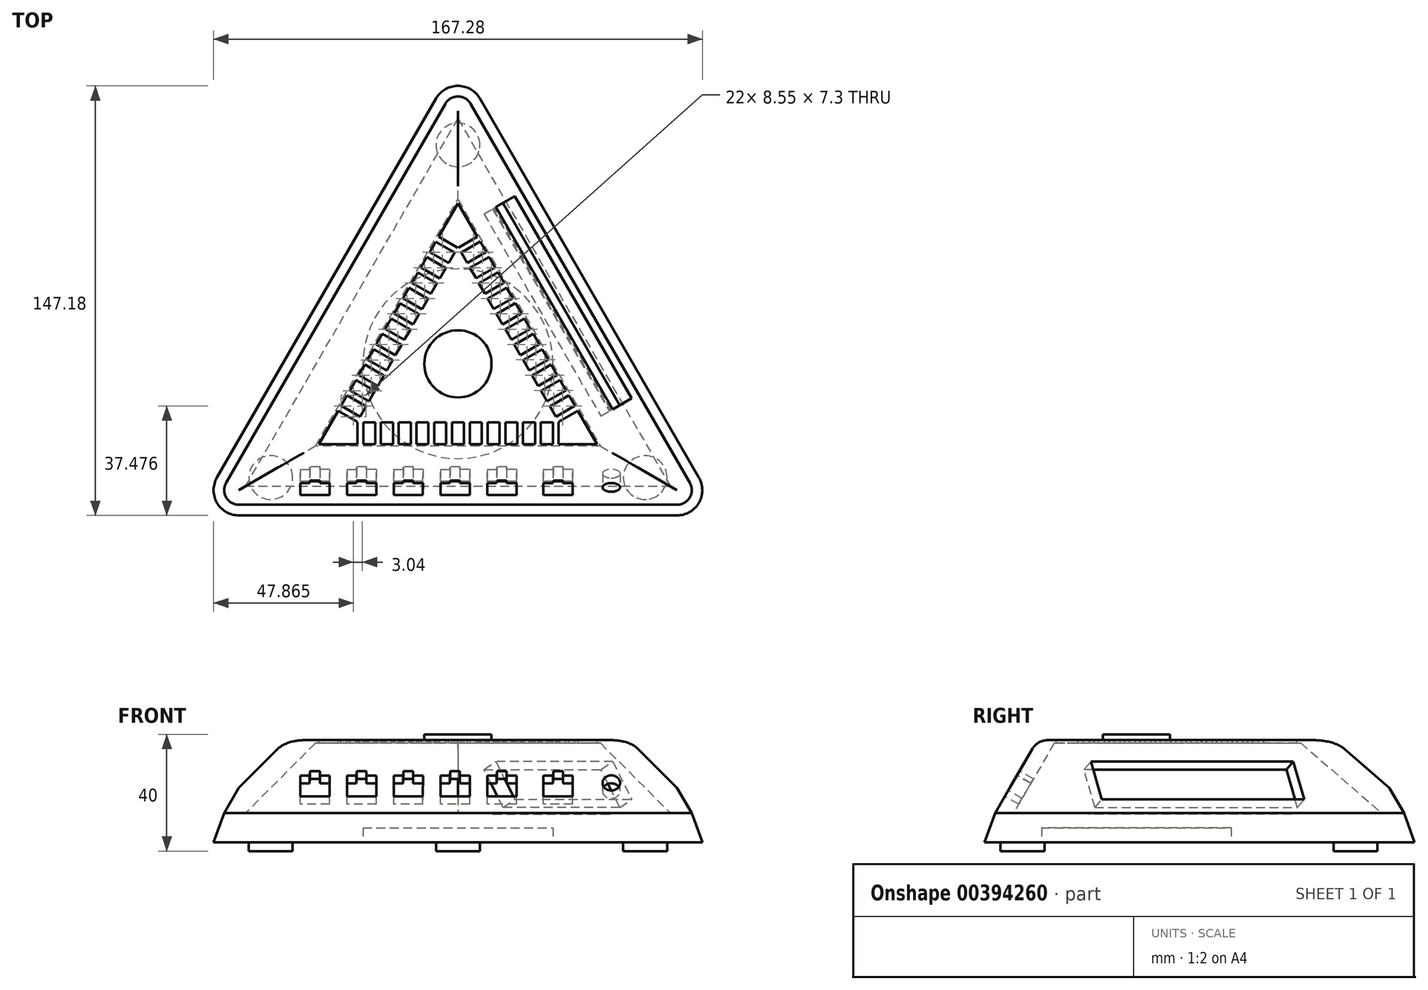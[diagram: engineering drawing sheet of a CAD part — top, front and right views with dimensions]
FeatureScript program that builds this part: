
annotation { "Feature Type Name" : "Feature", "Feature Type Description" : "" }
export const myFeature = defineFeature(function(context is Context, id is Id, definition is map)
    precondition{}
    {
        {
            var Q0;
            Q0=qCreatedBy(makeId("Top.planeOp"),FACE);
            var sketch = newSketch(context, id + "F0", { "sketchPlane" : qUnion([Q0])});
            skCircle(sketch, "E0.cCircle", {"center": v(0, 0) * mm, "radius": 48.3 * mm, "construction": true});
            skLineSegment(sketch, "E0.0", {"start": v(75, -48.3) * mm, "end": v(-75, -48.3) * mm});
            skLineSegment(sketch, "E0.1", {"start": v(-79.33, -40.8) * mm, "end": v(-4.33, 89.1) * mm});
            skLineSegment(sketch, "E0.2", {"start": v(4.33, 89.1) * mm, "end": v(79.33, -40.8) * mm});
            skPoint(sketch, "E0.0.midPoint", {"position": v(0, -48.3) * mm});
            skPoint(sketch, "E1.visualSharp", {"position": v(0, 96.6) * mm});
            skArc(sketch, "E1.filletArc", {"start": v(4.33, 89.1) * mm, "mid": v(0, 91.6) * mm, "end": v(-4.33, 89.1) * mm});
            skPoint(sketch, "E2.visualSharp", {"position": v(83.66, -48.3) * mm});
            skArc(sketch, "E2.filletArc", {"start": v(75, -48.3) * mm, "mid": v(79.33, -45.8) * mm, "end": v(79.33, -40.8) * mm});
            skPoint(sketch, "E3.visualSharp", {"position": v(-83.66, -48.3) * mm});
            skArc(sketch, "E3.filletArc", {"start": v(-79.33, -40.8) * mm, "mid": v(-79.33, -45.8) * mm, "end": v(-75, -48.3) * mm});
            skSolve(sketch);
        }
        {
            var Q0;
            Q0=makeQuery(id+"F0.imprint","IMPRINT",FACE,{"disambiguationData":[TD([[makeQuery(id+"F0.imprint","IMPRINT",EDGE,{"derivedFrom":sQuery(id+"F0.wireOp",EDGE,"E0.0")}),-1.0]])]});
            extrude(context, id + "F1", {"entities" : qUnion([Q0]), "depth" : 25 * mm, "hasDraft" : true, "draftAngle" : 30 * degree, "draftPullDirection" : true, "hasSecondDirection" : true, "secondDirectionOppositeDirection" : true, "secondDirectionDepth" : 10 * mm, "hasSecondDirectionDraft" : true, "secondDirectionDraftAngle" : 20 * degree});
        }
        {
            var Q0;
            Q0=makeQuery(id+"F1.opExtrude","CAP_EDGE",EDGE,{"disambiguationData":[OSD([sQuery(id+"F0.wireOp",EDGE,"E0.0")])],"isStart":false});
            var Q1;
            Q1=makeQuery(id+"F1.opExtrude","CAP_EDGE",EDGE,{"disambiguationData":[OSD([sQuery(id+"F0.wireOp",EDGE,"E0.2")])],"isStart":false});
            var Q2;
            Q2=makeQuery(id+"F1.opExtrude","CAP_EDGE",EDGE,{"disambiguationData":[OSD([sQuery(id+"F0.wireOp",EDGE,"E0.1")])],"isStart":false});
            fillet(context, id + "F2", {"entities" : qUnion([Q0, Q1, Q2]), "radius" : 6 * mm, "tangentPropagation" : true, "allowEdgeOverflow" : false});
        }
        {
            var Q0;
            Q0=makeQuery(id+"F1.opExtrude","CAP_FACE",FACE,{"disambiguationData":[OSD([sQuery(id+"F0.wireOp",EDGE,"E0.0"),sQuery(id+"F0.wireOp",EDGE,"E0.1"),sQuery(id+"F0.wireOp",EDGE,"E0.2"),sQuery(id+"F0.wireOp",EDGE,"E1.filletArc"),sQuery(id+"F0.wireOp",EDGE,"E2.filletArc"),sQuery(id+"F0.wireOp",EDGE,"E3.filletArc")])],"isStart":false});
            var sketch = newSketch(context, id + "F3", { "sketchPlane" : qUnion([Q0])});
            skCircle(sketch, "E4", {"center": v(0, 0) * mm, "radius": 11.5 * mm});
            skCircle(sketch, "E5.cCircle", {"center": v(0, 0) * mm, "radius": 20 * mm, "construction": true});
            skLineSegment(sketch, "E5.0", {"start": v(34.64, -20) * mm, "end": v(-34.64, -20) * mm});
            skLineSegment(sketch, "E5.1", {"start": v(-34.64, -20) * mm, "end": v(0, 40) * mm});
            skLineSegment(sketch, "E5.2", {"start": v(0, 40) * mm, "end": v(34.64, -20) * mm});
            skPoint(sketch, "E5.0.midPoint", {"position": v(0, -20) * mm});
            skCircle(sketch, "E6.cCircle", {"center": v(0, 0) * mm, "radius": 27.5 * mm, "construction": true});
            skLineSegment(sketch, "E6.0", {"start": v(47.63, -27.5) * mm, "end": v(-47.63, -27.5) * mm});
            skLineSegment(sketch, "E6.1", {"start": v(-47.63, -27.5) * mm, "end": v(0, 55) * mm});
            skLineSegment(sketch, "E6.2", {"start": v(0, 55) * mm, "end": v(47.63, -27.5) * mm});
            skPoint(sketch, "E6.0.midPoint", {"position": v(0, -27.5) * mm});
            skSolve(sketch);
        }
        {
            var Q0;
            Q0=makeQuery(id+"F3.imprint","IMPRINT",FACE,{"disambiguationData":[TD([[makeQuery(id+"F3.imprint","IMPRINT",EDGE,{"derivedFrom":sQuery(id+"F3.wireOp",EDGE,"E4")}),1.0]])]});
            extrude(context, id + "F4", {"entities" : qUnion([Q0]), "operationType" : NewBodyOperationType.ADD, "depth" : 2 * mm});
        }
        {
            var Q0;
            Q0=makeQuery(id+"F4.opExtrude","CAP_FACE",FACE,{"disambiguationData":[OSD([sQuery(id+"F3.wireOp",EDGE,"E4")])],"isStart":false});
            var sketch = newSketch(context, id + "F5", { "sketchPlane" : qUnion([Q0])});
            skSolve(sketch);
        }
        {
            var Q0;
            Q0=makeQuery(id+"F1.opExtrude","CAP_FACE",FACE,{"disambiguationData":[OSD([sQuery(id+"F0.wireOp",EDGE,"E0.0"),sQuery(id+"F0.wireOp",EDGE,"E0.1"),sQuery(id+"F0.wireOp",EDGE,"E0.2"),sQuery(id+"F0.wireOp",EDGE,"E1.filletArc"),sQuery(id+"F0.wireOp",EDGE,"E2.filletArc"),sQuery(id+"F0.wireOp",EDGE,"E3.filletArc")])],"isStart":true});
            var sketch = newSketch(context, id + "F6", { "sketchPlane" : qUnion([Q0])});
            skCircle(sketch, "E7", {"center": v(-64.07, 38.98) * mm, "radius": 7.5 * mm});
            skPoint(sketch, "E8.orphan", {"position": v(0, 0) * mm});
            skPoint(sketch, "E9.orphan", {"position": v(-82.48, 47.62) * mm});
            skCircle(sketch, "E10.MirrorC", {"center": v(64.07, 38.98) * mm, "radius": 7.5 * mm});
            skLineSegment(sketch, "E11", {"start": v(-64.07, 38.98) * mm, "end": v(0, 0) * mm});
            skCircle(sketch, "E12", {"center": v(0, -75) * mm, "radius": 7.5 * mm});
            skPoint(sketch, "E13.end.orphan", {"position": v(0, -95.24) * mm});
            skSolve(sketch);
        }
        {
            var Q0;
            Q0 = qSketchRegion(id + "F6", true);
            extrude(context, id + "F7", {"entities" : qUnion([Q0]), "operationType" : NewBodyOperationType.ADD, "depth" : 3 * mm});
        }
        {
            var Q0;
            Q0=makeQuery(id+"F1.opExtrude","CAP_FACE",FACE,{"disambiguationData":[OSD([sQuery(id+"F0.wireOp",EDGE,"E0.0"),sQuery(id+"F0.wireOp",EDGE,"E0.1"),sQuery(id+"F0.wireOp",EDGE,"E0.2"),sQuery(id+"F0.wireOp",EDGE,"E1.filletArc"),sQuery(id+"F0.wireOp",EDGE,"E2.filletArc"),sQuery(id+"F0.wireOp",EDGE,"E3.filletArc")])],"isStart":true});
            var sketch = newSketch(context, id + "F8", { "sketchPlane" : qUnion([Q0])});
            skCircle(sketch, "E14", {"center": v(0, 0) * mm, "radius": 32.5 * mm});
            skSolve(sketch);
        }
        {
            var Q0;
            Q0 = qSketchRegion(id + "F8", true);
            extrude(context, id + "F9", {"entities" : qUnion([Q0]), "operationType" : NewBodyOperationType.REMOVE, "oppositeDirection" : true, "depth" : 5 * mm});
        }
        {
            var Q0;
            Q0=makeQuery(id+"F1.*.split.splitOp","SPLIT",FACE,{"derivedFrom":makeQuery(id+"F1.opExtrude","SWEPT_FACE",FACE,{"disambiguationData":[OSD([sQuery(id+"F0.wireOp",EDGE,"E0.0")])]})});
            var sketch = newSketch(context, id + "F10", { "sketchPlane" : qUnion([Q0])});
            skLineSegment(sketch, "E15.top", {"start": v(-53.99, -17.5) * mm, "end": v(-43.99, -17.5) * mm});
            skLineSegment(sketch, "E16", {"start": v(-53.99, -9.3) * mm, "end": v(-53.99, -17.5) * mm});
            skLineSegment(sketch, "E17", {"start": v(-43.96, -9.24) * mm, "end": v(-43.99, -17.5) * mm});
            skLineSegment(sketch, "E18", {"start": v(-50.6, -7.5) * mm, "end": v(-47.3, -7.5) * mm});
            skLineSegment(sketch, "E19", {"start": v(-50.6, -7.5) * mm, "end": v(-50.74, -9.3) * mm});
            skLineSegment(sketch, "E20", {"start": v(-50.74, -9.3) * mm, "end": v(-53.99, -9.3) * mm});
            skLineSegment(sketch, "E21", {"start": v(-47.3, -7.5) * mm, "end": v(-47.3, -9.3) * mm});
            skLineSegment(sketch, "E22", {"start": v(-47.3, -9.3) * mm, "end": v(-43.96, -9.24) * mm});
            skPoint(sketch, "E15.left.start.orphan", {"position": v(-53.99, -7.5) * mm});
            skPoint(sketch, "E15.right.start.orphan", {"position": v(-43.99, -7.5) * mm});
            skLineSegment(sketch, "E23.1.0.0", {"start": v(-37.99, -9.3) * mm, "end": v(-37.99, -17.5) * mm});
            skLineSegment(sketch, "E23.1.0.1", {"start": v(-27.96, -9.24) * mm, "end": v(-27.99, -17.5) * mm});
            skPoint(sketch, "E23.1.0.2", {"position": v(-37.99, -7.5) * mm});
            skPoint(sketch, "E23.1.0.3", {"position": v(-27.99, -7.5) * mm});
            skLineSegment(sketch, "E23.1.0.4", {"start": v(-37.99, -17.5) * mm, "end": v(-27.99, -17.5) * mm});
            skLineSegment(sketch, "E23.1.0.5", {"start": v(-34.6, -7.5) * mm, "end": v(-31.3, -7.5) * mm});
            skLineSegment(sketch, "E23.1.0.6", {"start": v(-31.3, -7.5) * mm, "end": v(-31.3, -9.3) * mm});
            skLineSegment(sketch, "E23.1.0.7", {"start": v(-34.6, -7.5) * mm, "end": v(-34.74, -9.3) * mm});
            skLineSegment(sketch, "E23.1.0.8", {"start": v(-34.74, -9.3) * mm, "end": v(-37.99, -9.3) * mm});
            skLineSegment(sketch, "E23.1.0.9", {"start": v(-31.3, -9.3) * mm, "end": v(-27.96, -9.24) * mm});
            skLineSegment(sketch, "E23.2.0.0", {"start": v(-21.99, -9.3) * mm, "end": v(-21.99, -17.5) * mm});
            skLineSegment(sketch, "E23.2.0.1", {"start": v(-11.96, -9.24) * mm, "end": v(-11.99, -17.5) * mm});
            skPoint(sketch, "E23.2.0.2", {"position": v(-21.99, -7.5) * mm});
            skPoint(sketch, "E23.2.0.3", {"position": v(-11.99, -7.5) * mm});
            skLineSegment(sketch, "E23.2.0.4", {"start": v(-21.99, -17.5) * mm, "end": v(-11.99, -17.5) * mm});
            skLineSegment(sketch, "E23.2.0.5", {"start": v(-18.6, -7.5) * mm, "end": v(-15.3, -7.5) * mm});
            skLineSegment(sketch, "E23.2.0.6", {"start": v(-15.3, -7.5) * mm, "end": v(-15.3, -9.3) * mm});
            skLineSegment(sketch, "E23.2.0.7", {"start": v(-18.6, -7.5) * mm, "end": v(-18.74, -9.3) * mm});
            skLineSegment(sketch, "E23.2.0.8", {"start": v(-18.74, -9.3) * mm, "end": v(-21.99, -9.3) * mm});
            skLineSegment(sketch, "E23.2.0.9", {"start": v(-15.3, -9.3) * mm, "end": v(-11.96, -9.24) * mm});
            skLineSegment(sketch, "E23.3.0.0", {"start": v(-5.99, -9.3) * mm, "end": v(-5.99, -17.5) * mm});
            skLineSegment(sketch, "E23.3.0.1", {"start": v(4.04, -9.24) * mm, "end": v(4.01, -17.5) * mm});
            skPoint(sketch, "E23.3.0.2", {"position": v(-5.99, -7.5) * mm});
            skPoint(sketch, "E23.3.0.3", {"position": v(4.01, -7.5) * mm});
            skLineSegment(sketch, "E23.3.0.4", {"start": v(-5.99, -17.5) * mm, "end": v(4.01, -17.5) * mm});
            skLineSegment(sketch, "E23.3.0.5", {"start": v(-2.6, -7.5) * mm, "end": v(0.7, -7.5) * mm});
            skLineSegment(sketch, "E23.3.0.6", {"start": v(0.7, -7.5) * mm, "end": v(0.7, -9.3) * mm});
            skLineSegment(sketch, "E23.3.0.7", {"start": v(-2.6, -7.5) * mm, "end": v(-2.74, -9.3) * mm});
            skLineSegment(sketch, "E23.3.0.8", {"start": v(-2.74, -9.3) * mm, "end": v(-5.99, -9.3) * mm});
            skLineSegment(sketch, "E23.3.0.9", {"start": v(0.7, -9.3) * mm, "end": v(4.04, -9.24) * mm});
            skLineSegment(sketch, "E23.4.0.0", {"start": v(10.01, -9.3) * mm, "end": v(10.01, -17.5) * mm});
            skLineSegment(sketch, "E23.4.0.1", {"start": v(20.04, -9.24) * mm, "end": v(20.01, -17.5) * mm});
            skPoint(sketch, "E23.4.0.2", {"position": v(10.01, -7.5) * mm});
            skPoint(sketch, "E23.4.0.3", {"position": v(20.01, -7.5) * mm});
            skLineSegment(sketch, "E23.4.0.4", {"start": v(10.01, -17.5) * mm, "end": v(20.01, -17.5) * mm});
            skLineSegment(sketch, "E23.4.0.5", {"start": v(13.4, -7.5) * mm, "end": v(16.7, -7.5) * mm});
            skLineSegment(sketch, "E23.4.0.6", {"start": v(16.7, -7.5) * mm, "end": v(16.7, -9.3) * mm});
            skLineSegment(sketch, "E23.4.0.7", {"start": v(13.4, -7.5) * mm, "end": v(13.26, -9.3) * mm});
            skLineSegment(sketch, "E23.4.0.8", {"start": v(13.26, -9.3) * mm, "end": v(10.01, -9.3) * mm});
            skLineSegment(sketch, "E23.4.0.9", {"start": v(16.7, -9.3) * mm, "end": v(20.04, -9.24) * mm});
            skLineSegment(sketch, "E23.5.0.0", {"start": v(29.26, -9.3) * mm, "end": v(29.26, -17.5) * mm});
            skLineSegment(sketch, "E23.5.0.1", {"start": v(39.3, -9.24) * mm, "end": v(39.26, -17.5) * mm});
            skPoint(sketch, "E23.5.0.2", {"position": v(29.26, -7.5) * mm});
            skPoint(sketch, "E23.5.0.3", {"position": v(39.26, -7.5) * mm});
            skLineSegment(sketch, "E23.5.0.4", {"start": v(29.26, -17.5) * mm, "end": v(39.26, -17.5) * mm});
            skLineSegment(sketch, "E23.5.0.5", {"start": v(32.64, -7.5) * mm, "end": v(35.95, -7.5) * mm});
            skLineSegment(sketch, "E23.5.0.6", {"start": v(35.95, -7.5) * mm, "end": v(35.95, -9.3) * mm});
            skLineSegment(sketch, "E23.5.0.7", {"start": v(32.64, -7.5) * mm, "end": v(32.5, -9.3) * mm});
            skLineSegment(sketch, "E23.5.0.8", {"start": v(32.5, -9.3) * mm, "end": v(29.26, -9.3) * mm});
            skLineSegment(sketch, "E23.5.0.9", {"start": v(35.95, -9.3) * mm, "end": v(39.3, -9.24) * mm});
            skLineSegment(sketch, "E23.direction1", {"start": v(-53.99, -17.5) * mm, "end": v(-37.99, -17.5) * mm, "construction": true});
            skCircle(sketch, "E24", {"center": v(52.49, -12.2) * mm, "radius": 3 * mm});
            skSolve(sketch);
        }
        {
            var Q0;
            Q0 = qSketchRegion(id + "F10", true);
            extrude(context, id + "F11", {"entities" : qUnion([Q0]), "operationType" : NewBodyOperationType.REMOVE, "oppositeDirection" : true, "depth" : 2 * mm});
        }
        {
            var Q0;
            Q0=qCreatedBy(makeId("Front.planeOp"),FACE);
            var sketch = newSketch(context, id + "F12", { "sketchPlane" : qUnion([Q0])});
            skLineSegment(sketch, "E25", {"start": v(0, 27.54) * mm, "end": v(0, -12.74) * mm});
            skSolve(sketch);
        }
        {
            var Q0;
            Q0 = qSketchRegion(id + "F3", true);
            extrude(context, id + "F13", {"entities" : qUnion([Q0]), "operationType" : NewBodyOperationType.REMOVE, "oppositeDirection" : true, "depth" : 5 * mm});
        }
        {
            var Q0;
            Q0=makeQuery(id+"F13.boolean.opBoolean","SPLIT",FACE,{"disambiguationData":[TD([makeQuery(id+"F4.opExtrude","SWEPT_FACE",FACE,{"disambiguationData":[OSD([sQuery(id+"F3.wireOp",EDGE,"E4")])]})])],"derivedFrom":makeQuery(id+"F1.opExtrude","CAP_FACE",FACE,{"disambiguationData":[OSD([sQuery(id+"F0.wireOp",EDGE,"E0.0"),sQuery(id+"F0.wireOp",EDGE,"E0.1"),sQuery(id+"F0.wireOp",EDGE,"E0.2"),sQuery(id+"F0.wireOp",EDGE,"E1.filletArc"),sQuery(id+"F0.wireOp",EDGE,"E2.filletArc"),sQuery(id+"F0.wireOp",EDGE,"E3.filletArc")])],"isStart":false})});
            cPlane(context, id + "F14", {"entities" : qUnion([Q0]), "cplaneType" : CPlaneType.OFFSET, "offset" : 0 * mm, "oppositeDirection" : true, "width" : 150 * mm, "height" : 150 * mm});
        }
        {
            var Q0;
            Q0=qCreatedBy(id+"F14.planeOp",FACE);
            var sketch = newSketch(context, id + "F15", { "sketchPlane" : qUnion([Q0])});
            skLineSegment(sketch, "E26.bottom", {"start": v(-34.42, -19.8) * mm, "end": v(-32.44, -19.8) * mm});
            skLineSegment(sketch, "E26.top", {"start": v(-34.42, -28.4) * mm, "end": v(-32.44, -28.4) * mm});
            skLineSegment(sketch, "E26.left", {"start": v(-34.42, -19.8) * mm, "end": v(-34.42, -28.4) * mm});
            skLineSegment(sketch, "E26.right", {"start": v(-32.44, -19.8) * mm, "end": v(-32.44, -28.4) * mm});
            skLineSegment(sketch, "E27.1.0.0", {"start": v(-26.36, -19.8) * mm, "end": v(-26.36, -28.4) * mm});
            skLineSegment(sketch, "E27.1.0.1", {"start": v(-28.34, -19.8) * mm, "end": v(-28.34, -28.4) * mm});
            skLineSegment(sketch, "E27.1.0.2", {"start": v(-28.34, -28.4) * mm, "end": v(-26.36, -28.4) * mm});
            skLineSegment(sketch, "E27.1.0.3", {"start": v(-28.34, -19.8) * mm, "end": v(-26.36, -19.8) * mm});
            skLineSegment(sketch, "E27.2.0.0", {"start": v(-20.28, -19.8) * mm, "end": v(-20.28, -28.4) * mm});
            skLineSegment(sketch, "E27.2.0.1", {"start": v(-22.26, -19.8) * mm, "end": v(-22.26, -28.4) * mm});
            skLineSegment(sketch, "E27.2.0.2", {"start": v(-22.26, -28.4) * mm, "end": v(-20.28, -28.4) * mm});
            skLineSegment(sketch, "E27.2.0.3", {"start": v(-22.26, -19.8) * mm, "end": v(-20.28, -19.8) * mm});
            skLineSegment(sketch, "E27.3.0.0", {"start": v(-14.2, -19.8) * mm, "end": v(-14.2, -28.4) * mm});
            skLineSegment(sketch, "E27.3.0.1", {"start": v(-16.18, -19.8) * mm, "end": v(-16.18, -28.4) * mm});
            skLineSegment(sketch, "E27.3.0.2", {"start": v(-16.18, -28.4) * mm, "end": v(-14.2, -28.4) * mm});
            skLineSegment(sketch, "E27.3.0.3", {"start": v(-16.18, -19.8) * mm, "end": v(-14.2, -19.8) * mm});
            skLineSegment(sketch, "E27.4.0.0", {"start": v(-8.12, -19.8) * mm, "end": v(-8.12, -28.4) * mm});
            skLineSegment(sketch, "E27.4.0.1", {"start": v(-10.1, -19.8) * mm, "end": v(-10.1, -28.4) * mm});
            skLineSegment(sketch, "E27.4.0.2", {"start": v(-10.1, -28.4) * mm, "end": v(-8.12, -28.4) * mm});
            skLineSegment(sketch, "E27.4.0.3", {"start": v(-10.1, -19.8) * mm, "end": v(-8.12, -19.8) * mm});
            skLineSegment(sketch, "E27.5.0.0", {"start": v(-2.04, -19.8) * mm, "end": v(-2.04, -28.4) * mm});
            skLineSegment(sketch, "E27.5.0.1", {"start": v(-4.02, -19.8) * mm, "end": v(-4.02, -28.4) * mm});
            skLineSegment(sketch, "E27.5.0.2", {"start": v(-4.02, -28.4) * mm, "end": v(-2.04, -28.4) * mm});
            skLineSegment(sketch, "E27.5.0.3", {"start": v(-4.02, -19.8) * mm, "end": v(-2.04, -19.8) * mm});
            skLineSegment(sketch, "E27.6.0.0", {"start": v(4.04, -19.8) * mm, "end": v(4.04, -28.4) * mm});
            skLineSegment(sketch, "E27.6.0.1", {"start": v(2.06, -19.8) * mm, "end": v(2.06, -28.4) * mm});
            skLineSegment(sketch, "E27.6.0.2", {"start": v(2.06, -28.4) * mm, "end": v(4.04, -28.4) * mm});
            skLineSegment(sketch, "E27.6.0.3", {"start": v(2.06, -19.8) * mm, "end": v(4.04, -19.8) * mm});
            skLineSegment(sketch, "E27.7.0.0", {"start": v(10.12, -19.8) * mm, "end": v(10.12, -28.4) * mm});
            skLineSegment(sketch, "E27.7.0.1", {"start": v(8.14, -19.8) * mm, "end": v(8.14, -28.4) * mm});
            skLineSegment(sketch, "E27.7.0.2", {"start": v(8.14, -28.4) * mm, "end": v(10.12, -28.4) * mm});
            skLineSegment(sketch, "E27.7.0.3", {"start": v(8.14, -19.8) * mm, "end": v(10.12, -19.8) * mm});
            skLineSegment(sketch, "E27.8.0.0", {"start": v(16.2, -19.8) * mm, "end": v(16.2, -28.4) * mm});
            skLineSegment(sketch, "E27.8.0.1", {"start": v(14.22, -19.8) * mm, "end": v(14.22, -28.4) * mm});
            skLineSegment(sketch, "E27.8.0.2", {"start": v(14.22, -28.4) * mm, "end": v(16.2, -28.4) * mm});
            skLineSegment(sketch, "E27.8.0.3", {"start": v(14.22, -19.8) * mm, "end": v(16.2, -19.8) * mm});
            skLineSegment(sketch, "E27.9.0.0", {"start": v(22.28, -19.8) * mm, "end": v(22.28, -28.4) * mm});
            skLineSegment(sketch, "E27.9.0.1", {"start": v(20.3, -19.8) * mm, "end": v(20.3, -28.4) * mm});
            skLineSegment(sketch, "E27.9.0.2", {"start": v(20.3, -28.4) * mm, "end": v(22.28, -28.4) * mm});
            skLineSegment(sketch, "E27.9.0.3", {"start": v(20.3, -19.8) * mm, "end": v(22.28, -19.8) * mm});
            skLineSegment(sketch, "E27.10.0.0", {"start": v(28.36, -19.8) * mm, "end": v(28.36, -28.4) * mm});
            skLineSegment(sketch, "E27.10.0.1", {"start": v(26.38, -19.8) * mm, "end": v(26.38, -28.4) * mm});
            skLineSegment(sketch, "E27.10.0.2", {"start": v(26.38, -28.4) * mm, "end": v(28.36, -28.4) * mm});
            skLineSegment(sketch, "E27.10.0.3", {"start": v(26.38, -19.8) * mm, "end": v(28.36, -19.8) * mm});
            skLineSegment(sketch, "E27.11.0.0", {"start": v(34.44, -19.8) * mm, "end": v(34.44, -28.4) * mm});
            skLineSegment(sketch, "E27.11.0.1", {"start": v(32.46, -19.8) * mm, "end": v(32.46, -28.4) * mm});
            skLineSegment(sketch, "E27.11.0.2", {"start": v(32.46, -28.4) * mm, "end": v(34.44, -28.4) * mm});
            skLineSegment(sketch, "E27.11.0.3", {"start": v(32.46, -19.8) * mm, "end": v(34.44, -19.8) * mm});
            skLineSegment(sketch, "E27.direction1", {"start": v(-34.42, -28.4) * mm, "end": v(-28.34, -28.4) * mm, "construction": true});
            skLineSegment(sketch, "E28.1.0", {"start": v(18.16, 8.13) * mm, "end": v(25.6, 12.43) * mm});
            skLineSegment(sketch, "E28.1.1", {"start": v(15.12, 13.4) * mm, "end": v(22.57, 17.7) * mm});
            skLineSegment(sketch, "E28.1.2", {"start": v(2.96, 34.46) * mm, "end": v(10.4, 38.76) * mm});
            skLineSegment(sketch, "E28.1.3", {"start": v(12.08, 18.66) * mm, "end": v(19.53, 22.97) * mm});
            skLineSegment(sketch, "E28.1.4", {"start": v(-0.08, 39.73) * mm, "end": v(7.37, 44.03) * mm});
            skLineSegment(sketch, "E28.1.5", {"start": v(10.03, 22.21) * mm, "end": v(17.48, 26.52) * mm});
            skLineSegment(sketch, "E28.1.6", {"start": v(24.24, -2.4) * mm, "end": v(31.69, 1.9) * mm});
            skLineSegment(sketch, "E28.1.7", {"start": v(28.27, -9.38) * mm, "end": v(35.72, -5.08) * mm});
            skLineSegment(sketch, "E28.1.8", {"start": v(27.28, -7.66) * mm, "end": v(34.73, -3.36) * mm});
            skLineSegment(sketch, "E28.1.9", {"start": v(31.3, -14.64) * mm, "end": v(38.76, -10.34) * mm});
            skLineSegment(sketch, "E28.1.10", {"start": v(30.32, -12.93) * mm, "end": v(37.77, -8.63) * mm});
            skLineSegment(sketch, "E28.1.11", {"start": v(33.36, -18.2) * mm, "end": v(40.8, -13.9) * mm});
            skLineSegment(sketch, "E28.1.12", {"start": v(34.35, -19.9) * mm, "end": v(41.8, -15.6) * mm});
            skLineSegment(sketch, "E28.1.13", {"start": v(22.19, 1.15) * mm, "end": v(29.64, 5.45) * mm});
            skLineSegment(sketch, "E28.1.14", {"start": v(6.99, 27.48) * mm, "end": v(14.44, 31.78) * mm});
            skLineSegment(sketch, "E28.1.15", {"start": v(19.15, 6.42) * mm, "end": v(26.6, 10.72) * mm});
            skLineSegment(sketch, "E28.1.16", {"start": v(25.23, -4.11) * mm, "end": v(32.68, 0.19) * mm});
            skLineSegment(sketch, "E28.1.17", {"start": v(9.04, 23.93) * mm, "end": v(16.49, 28.23) * mm});
            skLineSegment(sketch, "E28.1.18", {"start": v(21.2, 2.87) * mm, "end": v(28.65, 7.17) * mm});
            skLineSegment(sketch, "E28.1.19", {"start": v(6, 29.2) * mm, "end": v(13.45, 33.5) * mm});
            skLineSegment(sketch, "E28.1.20", {"start": v(13.07, 16.95) * mm, "end": v(20.52, 21.25) * mm});
            skLineSegment(sketch, "E28.1.21", {"start": v(0.9, 38.01) * mm, "end": v(8.36, 42.31) * mm});
            skLineSegment(sketch, "E28.1.22", {"start": v(3.95, 32.75) * mm, "end": v(11.4, 37.05) * mm});
            skLineSegment(sketch, "E28.1.23", {"start": v(16.1, 11.68) * mm, "end": v(23.56, 15.99) * mm});
            skLineSegment(sketch, "E28.1.24", {"start": v(34.35, -19.9) * mm, "end": v(33.36, -18.2) * mm});
            skLineSegment(sketch, "E28.1.25", {"start": v(17.48, 26.52) * mm, "end": v(16.49, 28.23) * mm});
            skLineSegment(sketch, "E28.1.26", {"start": v(29.64, 5.45) * mm, "end": v(28.65, 7.17) * mm});
            skLineSegment(sketch, "E28.1.27", {"start": v(14.44, 31.78) * mm, "end": v(13.45, 33.5) * mm});
            skLineSegment(sketch, "E28.1.28", {"start": v(13.07, 16.95) * mm, "end": v(12.08, 18.66) * mm});
            skLineSegment(sketch, "E28.1.29", {"start": v(0.9, 38.01) * mm, "end": v(-0.08, 39.73) * mm});
            skLineSegment(sketch, "E28.1.30", {"start": v(26.6, 10.72) * mm, "end": v(25.6, 12.43) * mm});
            skLineSegment(sketch, "E28.1.31", {"start": v(28.27, -9.38) * mm, "end": v(27.28, -7.66) * mm});
            skLineSegment(sketch, "E28.1.32", {"start": v(31.3, -14.64) * mm, "end": v(30.32, -12.93) * mm});
            skLineSegment(sketch, "E28.1.33", {"start": v(38.76, -10.34) * mm, "end": v(37.77, -8.63) * mm});
            skLineSegment(sketch, "E28.1.34", {"start": v(41.8, -15.6) * mm, "end": v(40.8, -13.9) * mm});
            skLineSegment(sketch, "E28.1.35", {"start": v(25.23, -4.11) * mm, "end": v(24.24, -2.4) * mm});
            skLineSegment(sketch, "E28.1.36", {"start": v(20.52, 21.25) * mm, "end": v(19.53, 22.97) * mm});
            skLineSegment(sketch, "E28.1.37", {"start": v(8.36, 42.31) * mm, "end": v(7.37, 44.03) * mm});
            skLineSegment(sketch, "E28.1.38", {"start": v(32.68, 0.19) * mm, "end": v(31.69, 1.9) * mm});
            skLineSegment(sketch, "E28.1.39", {"start": v(16.1, 11.68) * mm, "end": v(15.12, 13.4) * mm});
            skLineSegment(sketch, "E28.1.40", {"start": v(3.95, 32.75) * mm, "end": v(2.96, 34.46) * mm});
            skLineSegment(sketch, "E28.1.41", {"start": v(41.8, -15.6) * mm, "end": v(38.76, -10.34) * mm, "construction": true});
            skLineSegment(sketch, "E28.1.42", {"start": v(19.15, 6.42) * mm, "end": v(18.16, 8.13) * mm});
            skLineSegment(sketch, "E28.1.43", {"start": v(6.99, 27.48) * mm, "end": v(6, 29.2) * mm});
            skLineSegment(sketch, "E28.1.44", {"start": v(23.56, 15.99) * mm, "end": v(22.57, 17.7) * mm});
            skLineSegment(sketch, "E28.1.45", {"start": v(11.4, 37.05) * mm, "end": v(10.4, 38.76) * mm});
            skLineSegment(sketch, "E28.1.46", {"start": v(22.19, 1.15) * mm, "end": v(21.2, 2.87) * mm});
            skLineSegment(sketch, "E28.1.47", {"start": v(10.03, 22.21) * mm, "end": v(9.04, 23.93) * mm});
            skLineSegment(sketch, "E28.1.48", {"start": v(35.72, -5.08) * mm, "end": v(34.73, -3.36) * mm});
            skLineSegment(sketch, "E28.2.0", {"start": v(-16.12, 11.66) * mm, "end": v(-23.57, 15.96) * mm});
            skLineSegment(sketch, "E28.2.1", {"start": v(-19.16, 6.4) * mm, "end": v(-26.61, 10.7) * mm});
            skLineSegment(sketch, "E28.2.2", {"start": v(-31.32, -14.67) * mm, "end": v(-38.77, -10.37) * mm});
            skLineSegment(sketch, "E28.2.3", {"start": v(-22.2, 1.13) * mm, "end": v(-29.65, 5.43) * mm});
            skLineSegment(sketch, "E28.2.4", {"start": v(-34.36, -19.93) * mm, "end": v(-41.81, -15.63) * mm});
            skLineSegment(sketch, "E28.2.5", {"start": v(-24.25, -2.42) * mm, "end": v(-31.7, 1.88) * mm});
            skLineSegment(sketch, "E28.2.6", {"start": v(-10.04, 22.2) * mm, "end": v(-17.5, 26.5) * mm});
            skLineSegment(sketch, "E28.2.7", {"start": v(-6.01, 29.17) * mm, "end": v(-13.46, 33.47) * mm});
            skLineSegment(sketch, "E28.2.8", {"start": v(-7, 27.46) * mm, "end": v(-14.45, 31.76) * mm});
            skLineSegment(sketch, "E28.2.9", {"start": v(-2.97, 34.44) * mm, "end": v(-10.42, 38.74) * mm});
            skLineSegment(sketch, "E28.2.10", {"start": v(-3.96, 32.72) * mm, "end": v(-11.41, 37.02) * mm});
            skLineSegment(sketch, "E28.2.11", {"start": v(-0.92, 37.99) * mm, "end": v(-8.37, 42.29) * mm});
            skLineSegment(sketch, "E28.2.12", {"start": v(0.07, 39.7) * mm, "end": v(-7.38, 44) * mm});
            skLineSegment(sketch, "E28.2.13", {"start": v(-12.1, 18.64) * mm, "end": v(-19.54, 22.94) * mm});
            skLineSegment(sketch, "E28.2.14", {"start": v(-27.3, -7.69) * mm, "end": v(-34.74, -3.39) * mm});
            skLineSegment(sketch, "E28.2.15", {"start": v(-15.13, 13.37) * mm, "end": v(-22.58, 17.68) * mm});
            skLineSegment(sketch, "E28.2.16", {"start": v(-9.05, 23.9) * mm, "end": v(-16.5, 28.2) * mm});
            skLineSegment(sketch, "E28.2.17", {"start": v(-25.24, -4.14) * mm, "end": v(-32.7, 0.16) * mm});
            skLineSegment(sketch, "E28.2.18", {"start": v(-13.08, 16.92) * mm, "end": v(-20.53, 21.23) * mm});
            skLineSegment(sketch, "E28.2.19", {"start": v(-28.28, -9.4) * mm, "end": v(-35.73, -5.1) * mm});
            skLineSegment(sketch, "E28.2.20", {"start": v(-21.21, 2.84) * mm, "end": v(-28.66, 7.14) * mm});
            skLineSegment(sketch, "E28.2.21", {"start": v(-33.37, -18.22) * mm, "end": v(-40.82, -13.92) * mm});
            skLineSegment(sketch, "E28.2.22", {"start": v(-30.33, -12.95) * mm, "end": v(-37.78, -8.65) * mm});
            skLineSegment(sketch, "E28.2.23", {"start": v(-18.17, 8.1) * mm, "end": v(-25.62, 12.4) * mm});
            skLineSegment(sketch, "E28.2.24", {"start": v(0.07, 39.7) * mm, "end": v(-0.92, 37.99) * mm});
            skLineSegment(sketch, "E28.2.25", {"start": v(-31.7, 1.88) * mm, "end": v(-32.7, 0.16) * mm});
            skLineSegment(sketch, "E28.2.26", {"start": v(-19.54, 22.94) * mm, "end": v(-20.53, 21.23) * mm});
            skLineSegment(sketch, "E28.2.27", {"start": v(-34.74, -3.39) * mm, "end": v(-35.73, -5.1) * mm});
            skLineSegment(sketch, "E28.2.28", {"start": v(-21.21, 2.84) * mm, "end": v(-22.2, 1.13) * mm});
            skLineSegment(sketch, "E28.2.29", {"start": v(-33.37, -18.22) * mm, "end": v(-34.36, -19.93) * mm});
            skLineSegment(sketch, "E28.2.30", {"start": v(-22.58, 17.68) * mm, "end": v(-23.57, 15.96) * mm});
            skLineSegment(sketch, "E28.2.31", {"start": v(-6.01, 29.17) * mm, "end": v(-7, 27.46) * mm});
            skLineSegment(sketch, "E28.2.32", {"start": v(-2.97, 34.44) * mm, "end": v(-3.96, 32.72) * mm});
            skLineSegment(sketch, "E28.2.33", {"start": v(-10.42, 38.74) * mm, "end": v(-11.41, 37.02) * mm});
            skLineSegment(sketch, "E28.2.34", {"start": v(-7.38, 44) * mm, "end": v(-8.37, 42.29) * mm});
            skLineSegment(sketch, "E28.2.35", {"start": v(-9.05, 23.9) * mm, "end": v(-10.04, 22.2) * mm});
            skLineSegment(sketch, "E28.2.36", {"start": v(-28.66, 7.14) * mm, "end": v(-29.65, 5.43) * mm});
            skLineSegment(sketch, "E28.2.37", {"start": v(-40.82, -13.92) * mm, "end": v(-41.81, -15.63) * mm});
            skLineSegment(sketch, "E28.2.38", {"start": v(-16.5, 28.2) * mm, "end": v(-17.5, 26.5) * mm});
            skLineSegment(sketch, "E28.2.39", {"start": v(-18.17, 8.1) * mm, "end": v(-19.16, 6.4) * mm});
            skLineSegment(sketch, "E28.2.40", {"start": v(-30.33, -12.95) * mm, "end": v(-31.32, -14.67) * mm});
            skLineSegment(sketch, "E28.2.41", {"start": v(-7.38, 44) * mm, "end": v(-10.42, 38.74) * mm, "construction": true});
            skLineSegment(sketch, "E28.2.42", {"start": v(-15.13, 13.37) * mm, "end": v(-16.12, 11.66) * mm});
            skLineSegment(sketch, "E28.2.43", {"start": v(-27.3, -7.69) * mm, "end": v(-28.28, -9.4) * mm});
            skLineSegment(sketch, "E28.2.44", {"start": v(-25.62, 12.4) * mm, "end": v(-26.61, 10.7) * mm});
            skLineSegment(sketch, "E28.2.45", {"start": v(-37.78, -8.65) * mm, "end": v(-38.77, -10.37) * mm});
            skLineSegment(sketch, "E28.2.46", {"start": v(-12.1, 18.64) * mm, "end": v(-13.08, 16.92) * mm});
            skLineSegment(sketch, "E28.2.47", {"start": v(-24.25, -2.42) * mm, "end": v(-25.24, -4.14) * mm});
            skLineSegment(sketch, "E28.2.48", {"start": v(-13.46, 33.47) * mm, "end": v(-14.45, 31.76) * mm});
            skPoint(sketch, "E28.center", {"position": v(0, 0) * mm});
            skSolve(sketch);
        }
        {
            var Q0;
            Q0 = qSketchRegion(id + "F15", true);
            extrude(context, id + "F16", {"entities" : qUnion([Q0]), "operationType" : NewBodyOperationType.ADD, "oppositeDirection" : true, "depth" : 1 * mm});
        }
        {
            var Q0;
            Q0 = qSketchRegion(id + "F10", true);
            extrude(context, id + "F17", {"entities" : qUnion([Q0]), "operationType" : NewBodyOperationType.REMOVE, "oppositeDirection" : true, "depth" : 10 * mm});
        }
        {
            var Q0;
            Q0=makeQuery(id+"F1.*.split.splitOp","SPLIT",FACE,{"derivedFrom":makeQuery(id+"F1.opExtrude","SWEPT_FACE",FACE,{"disambiguationData":[OSD([sQuery(id+"F0.wireOp",EDGE,"E0.2")])]})});
            var sketch = newSketch(context, id + "F18", { "sketchPlane" : qUnion([Q0])});
            skLineSegment(sketch, "E29", {"start": v(-37.4, -14.7) * mm, "end": v(39.47, 7.5) * mm});
            skLineSegment(sketch, "E30", {"start": v(43.63, -6.92) * mm, "end": v(-33.23, -29.1) * mm});
            skLineSegment(sketch, "E31", {"start": v(-37.4, -14.7) * mm, "end": v(-33.23, -29.1) * mm});
            skLineSegment(sketch, "E32.MirrorCS", {"start": v(39.47, 7.5) * mm, "end": v(43.63, -6.92) * mm});
            skSolve(sketch);
        }
        {
            var Q0;
            Q0 = qSketchRegion(id + "F18", true);
            var Q1;
            Q1=makeQuery(id+"F1.*.split.splitOp","SPLIT",FACE,{"derivedFrom":makeQuery(id+"F1.opExtrude","SWEPT_FACE",FACE,{"disambiguationData":[OSD([sQuery(id+"F0.wireOp",EDGE,"E0.0")])]})});
            extrude(context, id + "F19", {"entities" : qUnion([Q0]), "operationType" : NewBodyOperationType.REMOVE, "oppositeDirection" : true, "endBoundEntityFace" : qUnion([Q1]), "depth" : 10 * mm});
        }
        {
            var Q0;
            Q0=qCreatedBy(makeId("Top.planeOp"),FACE);
            var sketch = newSketch(context, id + "F20", { "sketchPlane" : qUnion([Q0])});
            skCircle(sketch, "E33.cCircle", {"center": v(0, 0) * mm, "radius": 42 * mm, "construction": true});
            skLineSegment(sketch, "E33.0", {"start": v(72.75, -42) * mm, "end": v(-72.75, -42) * mm});
            skLineSegment(sketch, "E33.1", {"start": v(-72.75, -42) * mm, "end": v(0, 84) * mm});
            skLineSegment(sketch, "E33.2", {"start": v(0, 84) * mm, "end": v(72.75, -42) * mm});
            skPoint(sketch, "E33.0.midPoint", {"position": v(0, -42) * mm});
            skSolve(sketch);
        }
        {
            var Q0;
            Q0 = qSketchRegion(id + "F20", true);
            extrude(context, id + "F21", {"entities" : qUnion([Q0]), "operationType" : NewBodyOperationType.REMOVE, "depth" : 24 * mm, "hasDraft" : true, "draftAngle" : 30 * degree, "draftPullDirection" : true});
        }
    });
